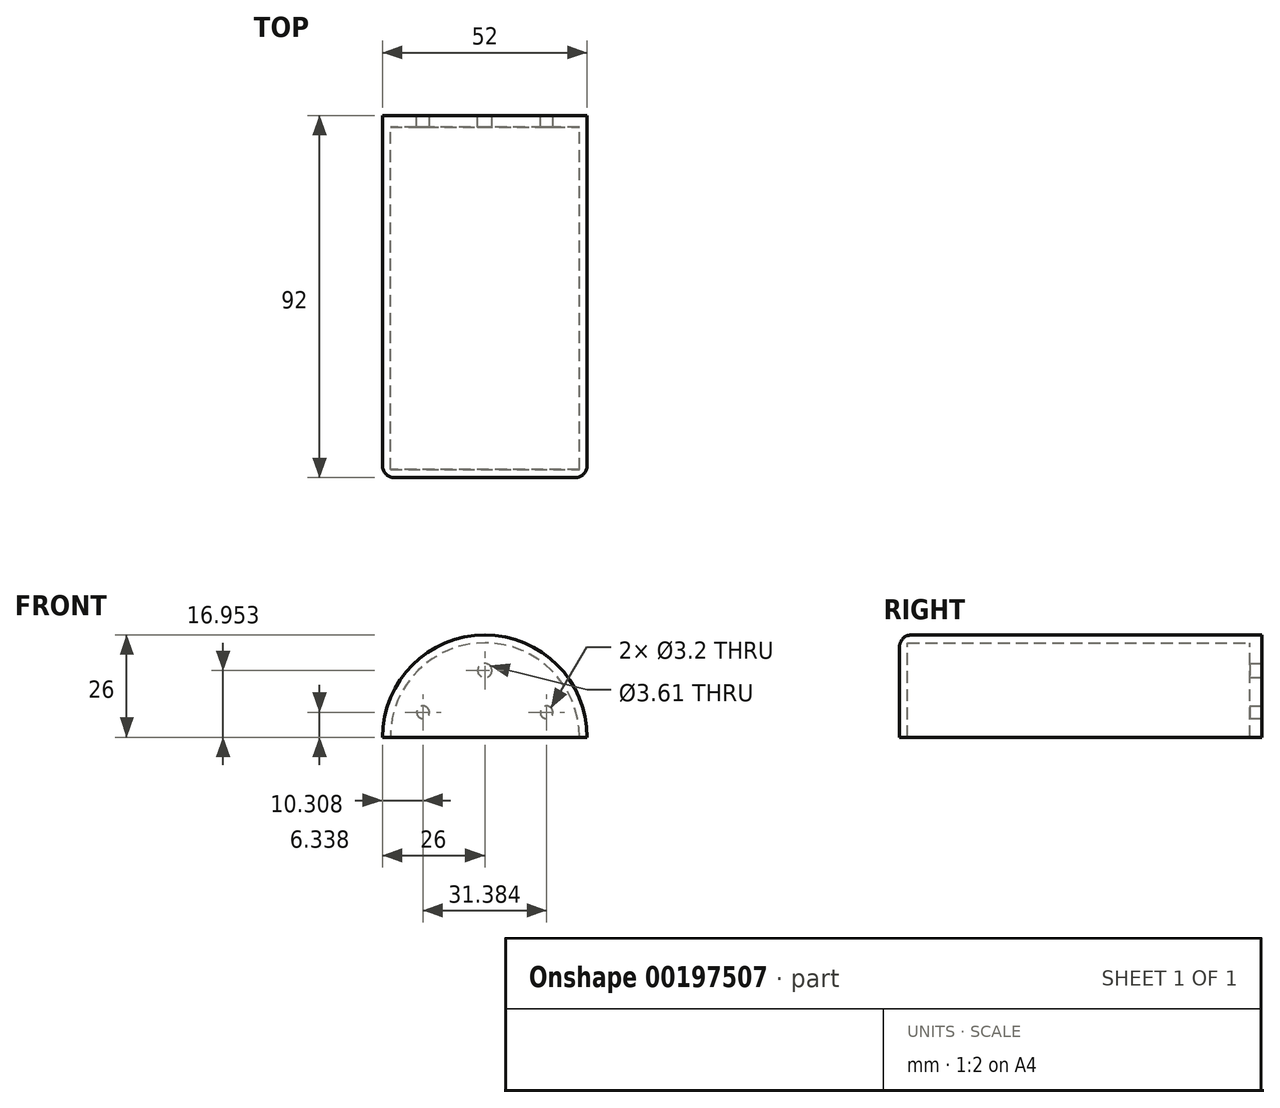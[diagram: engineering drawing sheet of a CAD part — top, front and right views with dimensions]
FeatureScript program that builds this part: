
annotation { "Feature Type Name" : "Feature", "Feature Type Description" : "" }
export const myFeature = defineFeature(function(context is Context, id is Id, definition is map)
    precondition{}
    {
        {
            var Q0;
            Q0=qCreatedBy(makeId("Front.planeOp"),FACE);
            var sketch = newSketch(context, id + "F0", { "sketchPlane" : qUnion([Q0])});
            skArc(sketch, "E0", {"start": v(26, 0) * mm, "mid": v(0, 26) * mm, "end": v(-26, 0) * mm});
            skArc(sketch, "E1", {"start": v(24, 0) * mm, "mid": v(0, 24) * mm, "end": v(-24, 0) * mm});
            skLineSegment(sketch, "E2", {"start": v(-26, 0) * mm, "end": v(-24, 0) * mm});
            skLineSegment(sketch, "E3.trimOffspring", {"start": v(24, 0) * mm, "end": v(26, 0) * mm});
            skSolve(sketch);
        }
        {
            var Q0;
            Q0=qSketchRegion(id+"F0",true);
            extrude(context, id + "F1", {"entities" : qUnion([Q0]), "depth" : 90 * mm});
        }
        {
            var Q0;
            Q0=makeQuery(id+"F1.opExtrude","CAP_FACE",FACE,{"disambiguationData":[OSD([sQuery(id+"F0.wireOp",EDGE,"E0"),sQuery(id+"F0.wireOp",EDGE,"E1"),sQuery(id+"F0.wireOp",EDGE,"E2"),sQuery(id+"F0.wireOp",EDGE,"E3.trimOffspring")])],"isStart":false});
            var sketch = newSketch(context, id + "F2", { "sketchPlane" : qUnion([Q0])});
            skArc(sketch, "E4.0", {"start": v(26, 0) * mm, "mid": v(0, 26) * mm, "end": v(-26, 0) * mm});
            skLineSegment(sketch, "E5", {"start": v(-26, 0) * mm, "end": v(26, 0) * mm});
            skSolve(sketch);
        }
        {
            var Q0;
            Q0=qSketchRegion(id+"F2",true);
            extrude(context, id + "F3", {"entities" : qUnion([Q0]), "operationType" : NewBodyOperationType.ADD, "depth" : 2 * mm});
        }
        {
            var Q0;
            Q0=makeQuery(id+"F3.opExtrude","CAP_EDGE",EDGE,{"disambiguationData":[OSD([sQuery(id+"F2.wireOp",EDGE,"E4.0")])],"isStart":false});
            fillet(context, id + "F4", {"entities" : qUnion([Q0]), "radius" : 3 * mm, "tangentPropagation" : true, "allowEdgeOverflow" : false});
        }
        {
            var Q0;
            Q0=qCreatedBy(makeId("Front.planeOp"),FACE);
            var sketch = newSketch(context, id + "F5", { "sketchPlane" : qUnion([Q0])});
            skArc(sketch, "E6.0", {"start": v(26, 0) * mm, "mid": v(0, 26) * mm, "end": v(-26, 0) * mm});
            skLineSegment(sketch, "E7.0", {"start": v(-26, 0) * mm, "end": v(26, 0) * mm});
            skPoint(sketch, "E8.orphan", {"position": v(24, 0) * mm});
            skPoint(sketch, "E9.orphan", {"position": v(-24, 0) * mm});
            skSolve(sketch);
        }
        {
            var Q0;
            Q0=qSketchRegion(id+"F5",true);
            extrude(context, id + "F6", {"entities" : qUnion([Q0]), "operationType" : NewBodyOperationType.ADD, "depth" : 3 * mm});
        }
        {
            var Q0;
            Q0=makeQuery(id+"F6.boolean.opBoolean","MERGE",FACE,{"derivedFrom":[makeQuery(id+"F1.opExtrude","CAP_FACE",FACE,{"disambiguationData":[OSD([sQuery(id+"F0.wireOp",EDGE,"E0"),sQuery(id+"F0.wireOp",EDGE,"E1"),sQuery(id+"F0.wireOp",EDGE,"E2"),sQuery(id+"F0.wireOp",EDGE,"E3.trimOffspring")])],"isStart":true}),makeQuery(id+"F6.opExtrude","CAP_FACE",FACE,{"disambiguationData":[OSD([sQuery(id+"F5.wireOp",EDGE,"E6.0"),sQuery(id+"F5.wireOp",EDGE,"E7.0")])],"isStart":true})]});
            var sketch = newSketch(context, id + "F7", { "sketchPlane" : qUnion([Q0])});
            skCircle(sketch, "E10", {"center": v(0, 16.95) * mm, "radius": 1.8 * mm});
            skCircle(sketch, "E11", {"center": v(15.7, 6.34) * mm, "radius": 1.6 * mm});
            skCircle(sketch, "E12.MirrorC", {"center": v(-15.7, 6.34) * mm, "radius": 1.6 * mm});
            skSolve(sketch);
        }
        {
            var Q0;
            Q0=qSketchRegion(id+"F7",true);
            extrude(context, id + "F8", {"entities" : qUnion([Q0]), "operationType" : NewBodyOperationType.REMOVE, "oppositeDirection" : true, "depth" : 3 * mm});
        }
    });
